# Revit family: Wenger Cabinet 28
name_source: partatom
category: Furniture
revit_build: Autodesk Revit Architecture 2012 (Build: 20110916_2132(x64)
units: mm (PartAtom-declared; Revit-internal decimal feet)

## types (4) — shared parameters
Cabinet Height = 5' - 9 3/4"
Manufacturer = Wenger Corporation
URL = http://www.wengercorp.com

## per-type parameters (varying)
| type | Cabinet Back Thickness | Cabinet Depth | Cabinet Label | Cabinet Width | Model |
| Standard Cabinet #28 | 0' - 0 3/4" | 3' - 3 1/4" | Labels : Standard | 2' - 3 1/2" | 28 |
| Acoustic Cabinet #28 | 0' - 3 1/4" | 3' - 5 3/4" | Labels : Acoustic | 2' - 3 1/2" | 28A |
| Narrow Acoustic Cabinet #28 | 0' - 3 1/4" | 3' - 5 3/4" | Labels : Narrow Acoustic | 1' - 9 1/2" | 28NA |
| Narrow Cabinet #28 | 0' - 0 3/4" | 3' - 3 1/4" | Labels : Narrow | 1' - 9 1/2" | 28N |

note: column(s) folded — value = type name in every type: Description

## geometry (parser evidence)
native form markers: Blend x20, Sweep x4
no freeform markers — native parametric forms only
